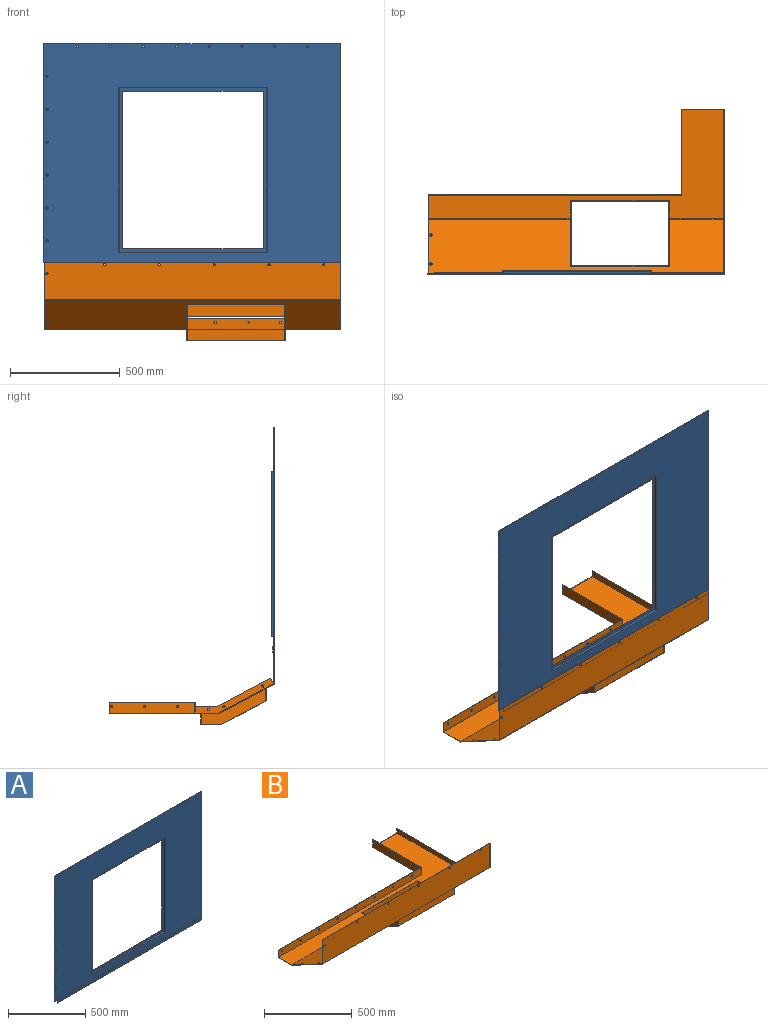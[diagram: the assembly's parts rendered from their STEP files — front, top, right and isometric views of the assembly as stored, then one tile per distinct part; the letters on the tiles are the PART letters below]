
ASSEMBLY  parts=2 mates=1
PART A: 46 faces, bbox 1352x14x1025.5 mm
  f0: plane 641.23x2mm, normal (0,0,1), area 1282.5mm2, adj f1,f2,f3,f4
  f1: plane 751.9x673.23mm, normal (0,-1,0), area 44580.2mm2, adj f0,f2,f4,f5,f6,f7,f8,f9
  f2: plane 719.9x2mm, normal (-1,0,0), area 1439.8mm2, adj f0,f1,f3,f9
  f3: plane 755.9x677.23mm, normal (0,1,0), area 50296.7mm2, adj f0,f2,f4,f9,f10,f11,f12,f13
  f4: plane 719.9x2mm, normal (1,0,0), area 1439.8mm2, adj f0,f1,f3,f9
  f5: plane 673.23x12mm, normal (0,0,-1), area 8078.8mm2, adj f1,f6,f8,f31
  f6: plane 751.9x12mm, normal (-1,0,0), area 9022.8mm2, adj f1,f5,f7,f31
  f7: plane 673.23x12mm, normal (0,0,1), area 8078.8mm2, adj f1,f6,f8,f31
  f8: plane 751.9x12mm, normal (1,0,0), area 9022.8mm2, adj f1,f5,f7,f31
  f9: plane 641.23x2mm, normal (0,0,-1), area 1282.5mm2, adj f1,f2,f3,f4
  f10: plane 677.23x12mm, normal (0,0,1), area 8126.8mm2, adj f3,f11,f13,f14
  f11: plane 755.9x12mm, normal (1,0,0), area 9070.8mm2, adj f3,f10,f12,f14
  f12: plane 677.23x12mm, normal (0,0,-1), area 8126.8mm2, adj f3,f11,f13,f14
  f13: plane 755.9x12mm, normal (-1,0,0), area 9070.8mm2, adj f3,f10,f12,f14
  f14: plane 1352x1000.5mm, normal (0,1,0), area 837013.1mm2, adj f10,f11,f12,f13,f15,f16,f17,f18
  f15: cylinder r=5mm len=10mm, axis (0,1,0), area 62.8mm2, adj f14,f31
  f16: cylinder r=5mm len=10mm, axis (0,1,0), area 62.8mm2, adj f14,f31
  f17: cylinder r=5mm len=10mm, axis (0,1,0), area 62.8mm2, adj f14,f31
  f18: cylinder r=5mm len=10mm, axis (0,1,0), area 62.8mm2, adj f14,f31
  f19: cylinder r=5mm len=10mm, axis (0,1,0), area 62.8mm2, adj f14,f31
  f20: cylinder r=5mm len=10mm, axis (0,1,0), area 62.8mm2, adj f14,f31
  f21: cylinder r=5mm len=10mm, axis (0,1,0), area 62.8mm2, adj f14,f31
  f22: cylinder r=5mm len=10mm, axis (0,1,0), area 62.8mm2, adj f14,f31
  f23: cylinder r=5mm len=10mm, axis (0,1,0), area 62.8mm2, adj f14,f31
  f24: cylinder r=5mm len=10mm, axis (0,1,0), area 62.8mm2, adj f14,f31
  f25: cylinder r=5mm len=10mm, axis (0,1,0), area 62.8mm2, adj f14,f31
  f26: cylinder r=5mm len=10mm, axis (0,1,0), area 62.8mm2, adj f14,f31
  f27: cylinder r=5mm len=10mm, axis (0,1,0), area 62.8mm2, adj f14,f31
  f28: cylinder r=5mm len=10mm, axis (0,1,0), area 62.8mm2, adj f14,f31
  f29: plane 1322x4mm, normal (0,0,1), area 5288mm2, adj f14,f33,f38,f39
  f30: plane 1322x2mm, normal (0,0,-1), area 2644mm2, adj f33,f36,f37,f39
  f31: plane 1352x1000.5mm, normal (0,-1,0), area 845373.6mm2, adj f5,f6,f7,f8,f15,f16,f17,f18
  f32: plane 1352x4mm, normal (0,0,-1), area 5348mm2, adj f14,f31,f33,f34,f36,f38
  f33: plane 1025.5x6mm, normal (1,0,0), area 2059mm2, adj f14,f29,f30,f31,f32,f35,f36,f39
  f34: plane 1000.5x2mm, normal (-1,0,0), area 2001mm2, adj f14,f31,f32,f35
  f35: plane 1352x2mm, normal (0,0,1), area 2704mm2, adj f14,f31,f33,f34
  f36: plane 1322x25mm, normal (0,-1,0), area 32646.1mm2, adj f30,f32,f33,f37,f38,f40,f41,f42
  f37: plane 12x2mm, normal (-1,0,0), area 24mm2, adj f30,f36,f39,f41
  f38: plane 7x4mm, normal (-1,0,0), area 18mm2, adj f14,f29,f32,f36,f39,f41
  f39: plane 1322x27mm, normal (0,1,0), area 35290.1mm2, adj f29,f30,f33,f37,f38,f40,f41,f42
  f40: cylinder r=5mm len=10mm, axis (0,1,0), area 62.8mm2, adj f36,f39
  f41: cylinder r=5mm len=8mm, axis (0,1,0), area 18.5mm2, adj f36,f37,f38,f39
  f42: cylinder r=5mm len=10mm, axis (0,1,0), area 62.8mm2, adj f36,f39
  f43: cylinder r=5mm len=10mm, axis (0,1,0), area 62.8mm2, adj f36,f39
  f44: cylinder r=5mm len=10mm, axis (0,1,0), area 62.8mm2, adj f36,f39
  f45: cylinder r=5mm len=10mm, axis (0,1,0), area 62.8mm2, adj f36,f39
PART B: 57 faces, bbox 1350x750.5x354 mm
  f0: plane 26.47x14.12mm, normal (0,-0.88,0.47), area 60mm2, adj f1,f2,f9,f11
  f1: plane 243.67x129.97mm, normal (0,0.47,0.88), area 552.3mm2, adj f0,f2,f11,f56
  f2: plane 748.5x159.97mm, normal (-1,0,0), area 22838.6mm2, adj f0,f1,f3,f4,f5,f6,f7,f12
  f3: cylinder r=5mm len=10mm, axis (-1,0,0), area 62.8mm2, adj f2,f11
  f4: cylinder r=5mm len=10mm, axis (-1,0,0), area 62.8mm2, adj f2,f11
  f5: cylinder r=5mm len=10mm, axis (-1,0,0), area 62.8mm2, adj f2,f11
  f6: cylinder r=5mm len=10mm, axis (-1,0,0), area 62.8mm2, adj f2,f11
  f7: cylinder r=5mm len=10mm, axis (-1,0,0), area 62.8mm2, adj f2,f11
  f8: cylinder r=5mm len=10mm, axis (0,1,0), area 62.8mm2, adj f9,f53
  f9: plane 1350x168.5mm, normal (0,1,0), area 227003.7mm2, adj f0,f8,f10,f11,f12,f13,f14,f15
  f10: plane 1350x2mm, normal (0,0,1), area 2700mm2, adj f9,f11,f13,f53
  f11: plane 750.5x304mm, normal (1,0,0), area 24742.8mm2, adj f0,f1,f3,f4,f5,f6,f7,f9
  f12: plane 1348x250.29mm, normal (0,0.47,0.88), area 273864.8mm2, adj f2,f9,f13,f19,f20,f21,f22,f23
  f13: plane 362.41x304mm, normal (-1,0,0), area 1228mm2, adj f9,f10,f12,f19,f29,f39,f41,f53
  f14: cylinder r=5mm len=10mm, axis (0,1,0), area 62.8mm2, adj f9,f53
  f15: cylinder r=5mm len=10mm, axis (0,1,0), area 62.8mm2, adj f9,f53
  f16: cylinder r=5mm len=10mm, axis (0,1,0), area 62.8mm2, adj f9,f53
  f17: cylinder r=5mm len=10mm, axis (0,1,0), area 62.8mm2, adj f9,f53
  f18: cylinder r=5mm len=10mm, axis (0,1,0), area 62.8mm2, adj f9,f53
  f19: plane 1348x498.21mm, normal (0,0,1), area 184135.1mm2, adj f2,f12,f13,f20,f22,f28,f29,f30
  f20: plane 296x166.34mm, normal (-1,0,0), area 16833.5mm2, adj f12,f19,f21,f30,f31,f32,f33
  f21: plane 446x57.87mm, normal (0,1,0), area 25809mm2, adj f12,f20,f22,f34
  f22: plane 296x166.34mm, normal (1,0,0), area 16833.5mm2, adj f12,f19,f21,f30,f31,f35,f36
  f23: cylinder r=5mm len=10mm, axis (0,0.47,0.88), area 62.8mm2, adj f12,f54
  f24: cylinder r=5mm len=10mm, axis (0,0.47,0.88), area 62.8mm2, adj f12,f54
  f25: plane 450x56.67mm, normal (0,-1,0), area 25500.5mm2, adj f26,f27,f34,f54
  f26: plane 300x165.14mm, normal (-1,0,0), area 16397.7mm2, adj f25,f31,f36,f37,f54,f55
  f27: plane 300x165.14mm, normal (1,0,0), area 16397.7mm2, adj f25,f31,f32,f37,f54,f55
  f28: plane 390.09x50mm, normal (1,0,0), area 19268.6mm2, adj f19,f29,f40,f41,f42,f43,f44
  f29: plane 1156.28x50mm, normal (0,-1,0), area 57185.7mm2, adj f13,f19,f28,f41,f45,f46,f47,f48
  f30: plane 446x52mm, normal (0,-1,0), area 23192mm2, adj f19,f20,f22,f31
  f31: plane 450x96.63mm, normal (0,0,-1), area 1278.5mm2, adj f20,f22,f26,f27,f30,f32,f36,f37
  f32: plane 203.37x108.48mm, normal (0,-0.47,-0.88), area 458.7mm2, adj f20,f27,f31,f33
  f33: plane 2x2mm, normal (-0.71,-0.71,0), area 1.5mm2, adj f20,f32,f34
  f34: plane 450x2mm, normal (0,0,-1), area 896mm2, adj f21,f25,f33,f35
  f35: plane 2x2mm, normal (0.71,-0.71,0), area 1.5mm2, adj f22,f34,f36
  f36: plane 203.37x108.48mm, normal (0,-0.47,-0.88), area 458.7mm2, adj f22,f26,f31,f35
  f37: plane 450x50mm, normal (0,1,0), area 22500mm2, adj f26,f27,f31,f55
  f38: plane 388.09x52mm, normal (-1,0,0), area 19944.8mm2, adj f39,f40,f41,f42,f43,f44,f55
  f39: plane 1154.28x52mm, normal (0,1,0), area 59394.2mm2, adj f13,f38,f41,f45,f46,f47,f48,f49
  f40: plane 195.72x52mm, normal (0,1,0), area 551.4mm2, adj f2,f11,f19,f28,f38,f41,f55,f56
  f41: plane 1156.28x390.09mm, normal (0,0,1), area 3088.7mm2, adj f13,f28,f29,f38,f39,f40
  f42: cylinder r=5mm len=10mm, axis (-1,0,0), area 62.8mm2, adj f28,f38
  f43: cylinder r=5mm len=10mm, axis (-1,0,0), area 62.8mm2, adj f28,f38
  f44: cylinder r=5mm len=10mm, axis (-1,0,0), area 62.8mm2, adj f28,f38
  f45: cylinder r=5mm len=10mm, axis (0,1,0), area 62.8mm2, adj f29,f39
  f46: cylinder r=5mm len=10mm, axis (0,1,0), area 62.8mm2, adj f29,f39
  f47: cylinder r=5mm len=10mm, axis (0,1,0), area 62.8mm2, adj f29,f39
  f48: cylinder r=5mm len=10mm, axis (0,1,0), area 62.8mm2, adj f29,f39
  f49: cylinder r=5mm len=10mm, axis (0,1,0), area 62.8mm2, adj f29,f39
  f50: cylinder r=5mm len=10mm, axis (0,1,0), area 62.8mm2, adj f29,f39
  f51: cylinder r=5mm len=10mm, axis (0,1,0), area 62.8mm2, adj f29,f39
  f52: cylinder r=5mm len=10mm, axis (0,1,0), area 62.8mm2, adj f29,f39
  f53: plane 1350x169.7mm, normal (0,-1,0), area 228623.7mm2, adj f8,f10,f11,f13,f14,f15,f16,f17
  f54: plane 1350x251.79mm, normal (0,-0.47,-0.88), area 274990.3mm2, adj f11,f13,f23,f24,f25,f26,f27,f53
  f55: plane 1350x498.71mm, normal (0,0,-1), area 187443.8mm2, adj f11,f13,f26,f27,f37,f38,f39,f40
  f56: plane 490.71x2mm, normal (0,0,1), area 981.4mm2, adj f1,f2,f11,f40
PLACE A t=(219.43,-385.13,340.69)mm fixed
PLACE B t=(219.43,-385.13,340.69)mm
MATE fastened B.f14 <-> A.f45  axis (0,1,0) through (142.43,-383.13,-666.81)mm
